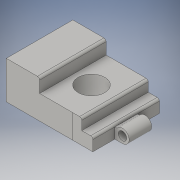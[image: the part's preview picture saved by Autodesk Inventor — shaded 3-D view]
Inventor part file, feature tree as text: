
AUTODESK INVENTOR PART (.ipt)
format: ipt  version: 2016 (Build 200138000, 138)  size: 254,976 bytes
history: native  units: in
note: dims shown in document units (in); Inventor stores cm internally (conversion verified against a paired STEP export)
features: extrude x18, sketch x16, reference x7, projected_geometry x3, plane x2, fillet x1
ambient origin geometry x8: Origin, YZ Plane, XZ Plane, XY Plane, X Axis, Y Axis, Z Axis, Center Point
bodies: Solid1 (feature_tree)
feature tree (47):
  extrude  "Extrusion1"  Depth=0.05in
  plane  "Work Plane1"
  extrude  "Extrusion5"  Depth=0.2362in
  plane  "Work Plane3"
  extrude  "Extrusion6"  [1 undecoded]
  extrude  "Extrusion8"  [1 undecoded]
  extrude  "Extrusion9"  Depth=0.4in TaperAngle=0.0deg
  extrude  "Extrusion10"  Depth=0.4in TaperAngle=0.0deg
  extrude  "Extrusion11"  Depth=0.3937in
  extrude  "Extrusion12"  Depth=0.05in TaperAngle=0.0deg
  extrude  "Extrusion13"  Depth=0.3937in TaperAngle=0.0deg
  extrude  "Extrusion14"  Depth=0.3937in TaperAngle=0.0deg
  extrude  "Extrusion15"  Depth=0.1969in TaperAngle=0.0deg
  extrude  "Extrusion16"  Depth=1.1801in
  extrude  "Extrusion17"  Depth=1.1801in
  extrude  "Extrusion18"  Depth=0.0394in TaperAngle=0.0deg
  extrude  "Extrusion19"  Depth=0.0394in
  extrude  "Extrusion20"  [1 undecoded]
  extrude  "Extrusion21"  [1 undecoded]
  extrude  "Extrusion22"  [1 undecoded]
  fillet  "Fillet1"  [1 undecoded]
  sketch  "Sketch1"  dims[d0=0.15in d1=0.05in]
  sketch  "Sketch2"  dims[d2=0.2362in d3=0.1496in]
  sketch  "Sketch6"  dims[d4=1.2in d5=0.0in d6=-0.4in]
  sketch  "Sketch8"  dims[d19=1.0in d20=0.0in d21=-0.4in]
  sketch  "Sketch9"  dims[d22=1.0in d23=0.0in d26=0.4in d27=0.0in]
  projected_geometry  "Projected Loop1"
  sketch  "Sketch10"  dims[d28=0.4in d29=0.0in d30=0.4in d31=0.0in]
  sketch  "Sketch11"  dims[d32=0.4in d33=0.0in d34=0.3937in]
  sketch  "Sketch12"  dims[d35=0.05in d36=0.0in d37=0.05in d38=0.0in]
  sketch  "Sketch13"  dims[d39=0.1772in d40=0.3937in d41=0.0in]
  reference  "Reference1"
  reference  "Reference2"
  sketch  "Sketch15"  dims[d42=0.0098in d43=0.3937in d44=0.0in]
  sketch  "Sketch16"  dims[d45=0.3937in d46=0.0in d47=0.1969in d48=0.0in]
  projected_geometry  "Projected Loop2"
  sketch  "Sketch17"  dims[d49=1.1801in d50=0.0in d51=0.4724in]
  reference  "Reference3"
  sketch  "Sketch18"  dims[d52=1.1801in d53=0.0in d54=0.0197in]
  reference  "Reference4"
  reference  "Reference5"
  reference  "Reference6"
  reference  "Reference7"
  sketch  "Sketch20"  dims[d55=23.0in d56=0.0in d57=0.0394in d58=0.0in]
  sketch  "Sketch21"  dims[d59=0.0394in d60=0.0in d61=0.0394in]
  projected_geometry  "Projected Loop3"
  sketch  "Sketch22"
note: 6 required parameter values undecoded (feature->parameter linkage not recoverable at this tier; creation-order binding heuristic only, values carry confidence <= 0.55)
